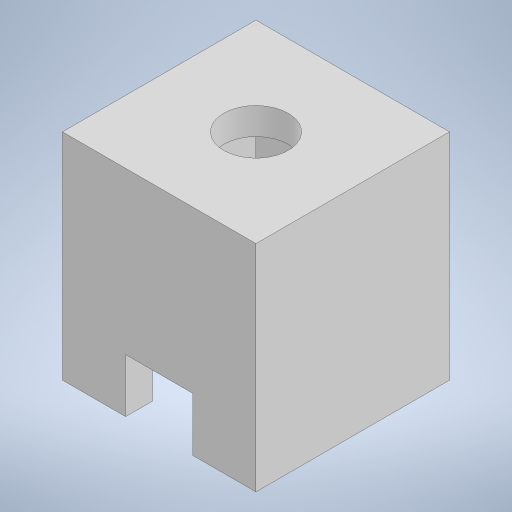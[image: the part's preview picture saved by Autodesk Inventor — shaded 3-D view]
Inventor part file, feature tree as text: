
AUTODESK INVENTOR PART (.ipt)
format: ipt  version: 2023 (Build 270158000, 158)  size: 202,752 bytes
history: native  units: in
note: dims shown in document units (in); Inventor stores cm internally (conversion verified against a paired STEP export)
features: extrude x3, sketch x3, projected_geometry x2
ambient origin geometry x8: Origin, YZ Plane, XZ Plane, XY Plane, X Axis, Y Axis, Z Axis, Center Point
bodies: Solid1 (feature_tree)
feature tree (8):
  extrude  "Extrusion1"  Depth=0.26in
  extrude  "Extrusion2"  Depth=0.13in
  extrude  "Extrusion3"  Depth=0.1in
  sketch  "Sketch1"  dims[d0=0.26in d1=0.26in]
  sketch  "Sketch2"  dims[d2=0.13in d3=0.13in]
  projected_geometry  "Projected Loop1"
  sketch  "Sketch3"  dims[d4=0.05in d5=0.0in d6=0.12in d7=0.05in d8=0.4in d9=0.0in d10=0.125in d11=0.36in d12=0.18in d13=0.1in d14=0.15in d15=0.0in]
  projected_geometry  "Projected Loop2"
